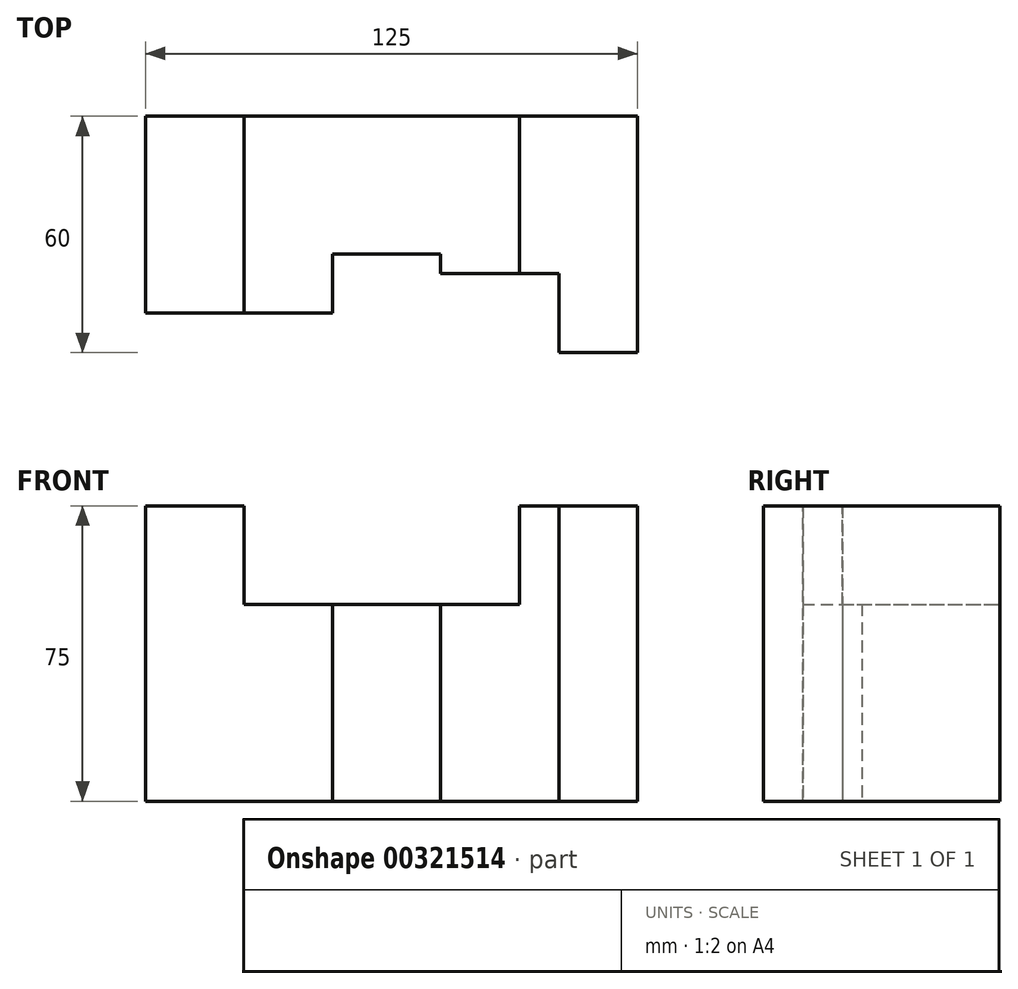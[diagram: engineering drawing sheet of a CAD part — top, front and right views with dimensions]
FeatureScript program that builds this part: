
annotation { "Feature Type Name" : "Feature", "Feature Type Description" : "" }
export const myFeature = defineFeature(function(context is Context, id is Id, definition is map)
    precondition{}
    {
        {
            var Q0;
            Q0=qCreatedBy(makeId("Front.planeOp"),FACE);
            var sketch = newSketch(context, id + "F0", { "sketchPlane" : qUnion([Q0])});
            skLineSegment(sketch, "E0", {"start": v(0, 0) * mm, "end": v(0, 75) * mm});
            skLineSegment(sketch, "E1", {"start": v(0, 75) * mm, "end": v(25, 75) * mm});
            skLineSegment(sketch, "E2", {"start": v(25, 75) * mm, "end": v(25, 50) * mm});
            skLineSegment(sketch, "E3", {"start": v(25, 50) * mm, "end": v(95, 50) * mm});
            skLineSegment(sketch, "E4", {"start": v(95, 50) * mm, "end": v(95, 75) * mm});
            skLineSegment(sketch, "E5", {"start": v(95, 75) * mm, "end": v(125, 75) * mm});
            skLineSegment(sketch, "E6", {"start": v(125, 75) * mm, "end": v(125, 0) * mm});
            skLineSegment(sketch, "E7", {"start": v(125, 0) * mm, "end": v(0, 0) * mm});
            skLineSegment(sketch, "E8", {"start": v(47.5, 50) * mm, "end": v(47.5, 0) * mm});
            skLineSegment(sketch, "E9", {"start": v(75, 50) * mm, "end": v(75, 0) * mm});
            skLineSegment(sketch, "E10", {"start": v(105, 75) * mm, "end": v(105, 0) * mm});
            skLineSegment(sketch, "E11", {"start": v(25, 50) * mm, "end": v(25, 0) * mm, "construction": true});
            skLineSegment(sketch, "E12", {"start": v(95, 50) * mm, "end": v(95, 0) * mm, "construction": true});
            skSolve(sketch);
        }
        {
            var Q0;
            {var subQ4=sQuery(id+"F0.wireOp",EDGE,"E0");Q0=makeQuery(id+"F0.imprint","IMPRINT",FACE,{"disambiguationData":[TD([[makeQuery(id+"F0.imprint","IMPRINT",EDGE,{"derivedFrom":subQ4}),-1.0]])]});}
            extrude(context, id + "F1", {"entities" : qUnion([Q0]), "depth" : 50 * mm});
        }
        {
            var Q0;
            {var subQ0=sQuery(id+"F0.wireOp",EDGE,"E8");Q0=makeQuery(id+"F0.imprint","IMPRINT",FACE,{"disambiguationData":[TD([[makeQuery(id+"F0.imprint","IMPRINT",EDGE,{"derivedFrom":subQ0}),1.0]])]});}
            extrude(context, id + "F2", {"entities" : qUnion([Q0]), "operationType" : NewBodyOperationType.ADD, "depth" : (7 * 5) * mm});
        }
        {
            var Q0;
            {var subQ1=sQuery(id+"F0.wireOp",EDGE,"E4");Q0=makeQuery(id+"F0.imprint","IMPRINT",FACE,{"disambiguationData":[TD([[makeQuery(id+"F0.imprint","IMPRINT",EDGE,{"derivedFrom":subQ1}),-1.0]])]});}
            extrude(context, id + "F3", {"entities" : qUnion([Q0]), "operationType" : NewBodyOperationType.ADD, "depth" : (8 * 5) * mm});
        }
        {
            var Q0;
            {var subQ0=sQuery(id+"F0.wireOp",EDGE,"E6");Q0=makeQuery(id+"F0.imprint","IMPRINT",FACE,{"disambiguationData":[TD([[makeQuery(id+"F0.imprint","IMPRINT",EDGE,{"derivedFrom":subQ0}),-1.0]])]});}
            extrude(context, id + "F4", {"entities" : qUnion([Q0]), "operationType" : NewBodyOperationType.ADD, "depth" : (12 * 5) * mm});
        }
    });
